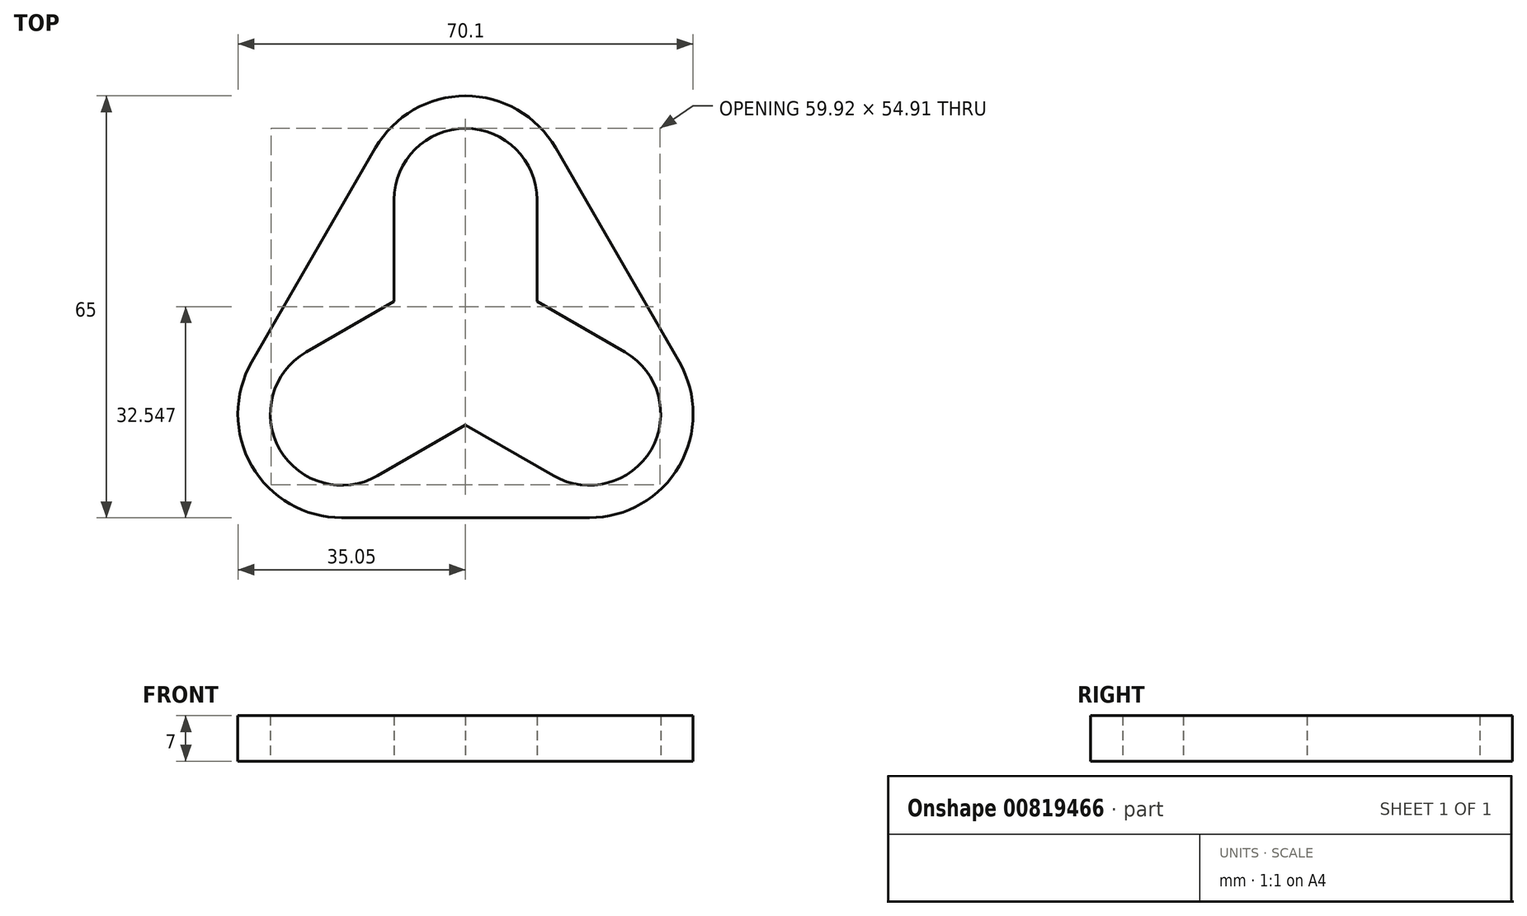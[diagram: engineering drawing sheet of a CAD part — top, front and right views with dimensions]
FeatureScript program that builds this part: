
annotation { "Feature Type Name" : "Feature", "Feature Type Description" : "" }
export const myFeature = defineFeature(function(context is Context, id is Id, definition is map)
    precondition{}
    {
        {
            var Q0;
            Q0=qCreatedBy(makeId("Top.planeOp"),FACE);
            var sketch = newSketch(context, id + "F0", { "sketchPlane" : qUnion([Q0])});
            skArc(sketch, "E0", {"start": v(9.53, 27.5) * mm, "mid": v(0, 33) * mm, "end": v(-9.53, 27.5) * mm});
            skArc(sketch, "E1.1.0", {"start": v(-28.58, -5.5) * mm, "mid": v(-28.58, -16.5) * mm, "end": v(-19.05, -22) * mm});
            skArc(sketch, "E1.2.0", {"start": v(19.05, -22) * mm, "mid": v(28.58, -16.5) * mm, "end": v(28.58, -5.5) * mm});
            skPoint(sketch, "E1.center", {"position": v(0, 0) * mm});
            skLineSegment(sketch, "E2", {"start": v(-9.53, 27.5) * mm, "end": v(-28.58, -5.5) * mm});
            skLineSegment(sketch, "E3", {"start": v(-19.05, -22) * mm, "end": v(19.05, -22) * mm});
            skLineSegment(sketch, "E4", {"start": v(28.58, -5.5) * mm, "end": v(9.53, 27.5) * mm});
            skArc(sketch, "E5.0", {"start": v(13.86, 30) * mm, "mid": v(0, 38) * mm, "end": v(-13.86, 30) * mm});
            skArc(sketch, "E5.1", {"start": v(-32.9, -3) * mm, "mid": v(-32.9, -19) * mm, "end": v(-19.05, -27) * mm});
            skLineSegment(sketch, "E5.2", {"start": v(-19.05, -27) * mm, "end": v(19.05, -27) * mm});
            skLineSegment(sketch, "E5.3", {"start": v(-13.86, 30) * mm, "end": v(-32.9, -3) * mm});
            skArc(sketch, "E5.4", {"start": v(19.05, -27) * mm, "mid": v(32.9, -19) * mm, "end": v(32.9, -3) * mm});
            skLineSegment(sketch, "E5.5", {"start": v(32.9, -3) * mm, "end": v(13.86, 30) * mm});
            skArc(sketch, "E6", {"start": v(-24.55, -1.47) * mm, "mid": v(-28.58, -16.5) * mm, "end": v(-13.55, -20.53) * mm});
            skArc(sketch, "E7", {"start": v(13.55, -20.53) * mm, "mid": v(28.58, -16.5) * mm, "end": v(24.55, -1.47) * mm});
            skArc(sketch, "E8", {"start": v(11, 22) * mm, "mid": v(0, 33) * mm, "end": v(-11, 22) * mm});
            skLineSegment(sketch, "E9", {"start": v(-11, 6.35) * mm, "end": v(-24.55, -1.47) * mm});
            skLineSegment(sketch, "E10", {"start": v(-13.55, -20.53) * mm, "end": v(0, -12.7) * mm});
            skLineSegment(sketch, "E11", {"start": v(0, -12.7) * mm, "end": v(13.55, -20.53) * mm});
            skLineSegment(sketch, "E12", {"start": v(11, 22) * mm, "end": v(11, 6.35) * mm});
            skLineSegment(sketch, "E13", {"start": v(24.55, -1.47) * mm, "end": v(11, 6.35) * mm});
            skLineSegment(sketch, "E14", {"start": v(-11, 22) * mm, "end": v(-11, 6.35) * mm});
            skSolve(sketch);
        }
        {
            var Q0;
            Q0 = qSketchRegion(id + "F0", true);
            var Q1;
            {var subQ2=sQuery(id+"F0.wireOp",EDGE,"E2");Q1=makeQuery(id+"F0.imprint","IMPRINT",FACE,{"disambiguationData":[TD([[makeQuery(id+"F0.imprint","IMPRINT",EDGE,{"derivedFrom":subQ2}),1.0]])]});}
            var Q2;
            {var subQ2=sQuery(id+"F0.wireOp",EDGE,"E4");Q2=makeQuery(id+"F0.imprint","IMPRINT",FACE,{"disambiguationData":[TD([[makeQuery(id+"F0.imprint","IMPRINT",EDGE,{"derivedFrom":subQ2}),1.0]])]});}
            var Q3;
            {var subQ2=sQuery(id+"F0.wireOp",EDGE,"E3");Q3=makeQuery(id+"F0.imprint","IMPRINT",FACE,{"disambiguationData":[TD([[makeQuery(id+"F0.imprint","IMPRINT",EDGE,{"derivedFrom":subQ2}),1.0]])]});}
            extrude(context, id + "F1", {"entities" : qUnion([Q0, Q1, Q2, Q3]), "depth" : 7 * mm, "offsetDistance" : 25.4 * mm});
        }
    });
